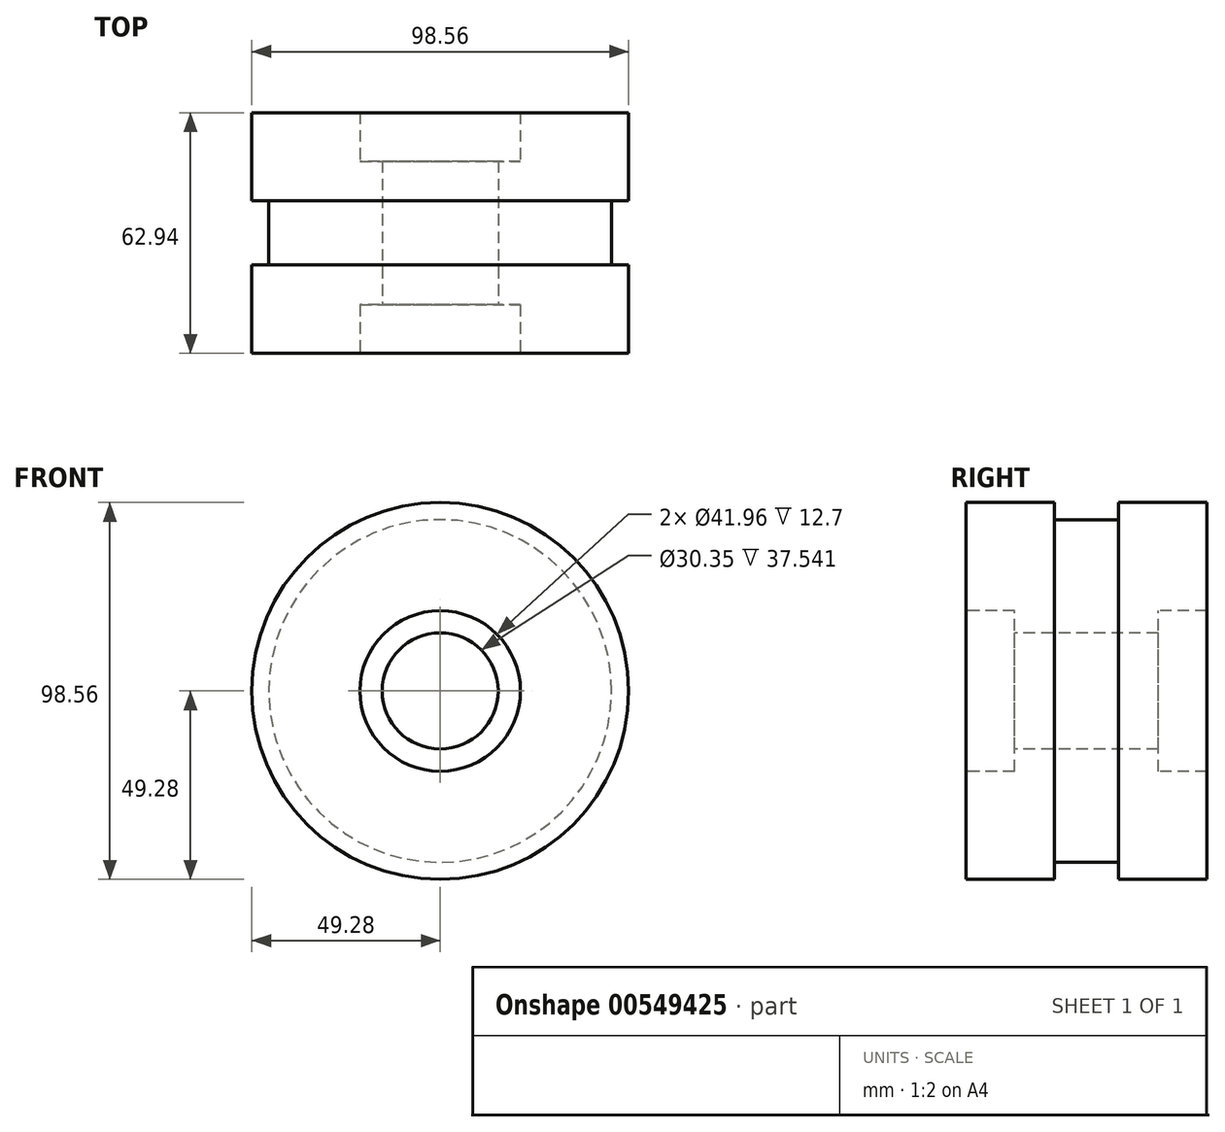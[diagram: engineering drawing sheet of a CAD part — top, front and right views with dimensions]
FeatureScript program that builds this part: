
annotation { "Feature Type Name" : "Feature", "Feature Type Description" : "" }
export const myFeature = defineFeature(function(context is Context, id is Id, definition is map)
    precondition{}
    {
        {
            var Q0;
            Q0=qCreatedBy(makeId("Right.planeOp"),FACE);
            var sketch = newSketch(context, id + "F0", { "sketchPlane" : qUnion([Q0])});
            skLineSegment(sketch, "E0", {"start": v(-35.21, 0) * mm, "end": v(33.24, 0) * mm, "construction": true});
            skLineSegment(sketch, "E1", {"start": v(0, 15.18) * mm, "end": v(-18.77, 15.18) * mm});
            skLineSegment(sketch, "E2", {"start": v(-18.77, 15.18) * mm, "end": v(-18.77, 20.98) * mm});
            skLineSegment(sketch, "E3", {"start": v(-18.77, 20.98) * mm, "end": v(-31.47, 20.98) * mm});
            skLineSegment(sketch, "E4", {"start": v(-31.47, 20.98) * mm, "end": v(-31.47, 49.28) * mm});
            skLineSegment(sketch, "E5", {"start": v(-31.47, 49.28) * mm, "end": v(-8.38, 49.28) * mm});
            skLineSegment(sketch, "E6", {"start": v(-8.38, 49.28) * mm, "end": v(-8.38, 44.8) * mm});
            skLineSegment(sketch, "E7", {"start": v(-8.38, 44.8) * mm, "end": v(8.38, 44.8) * mm});
            skLineSegment(sketch, "E8", {"start": v(0, 44.8) * mm, "end": v(0, 15.18) * mm, "construction": true});
            skLineSegment(sketch, "E9.MirrorCS", {"start": v(8.38, 49.28) * mm, "end": v(8.38, 44.8) * mm});
            skLineSegment(sketch, "E10.MirrorCS", {"start": v(31.47, 49.28) * mm, "end": v(8.38, 49.28) * mm});
            skLineSegment(sketch, "E11.MirrorCS", {"start": v(31.47, 20.98) * mm, "end": v(31.47, 49.28) * mm});
            skLineSegment(sketch, "E12.MirrorCS", {"start": v(18.77, 20.98) * mm, "end": v(31.47, 20.98) * mm});
            skLineSegment(sketch, "E13.MirrorCS", {"start": v(18.77, 15.18) * mm, "end": v(18.77, 20.98) * mm});
            skLineSegment(sketch, "E14.MirrorCS", {"start": v(0, 15.18) * mm, "end": v(18.77, 15.18) * mm});
            skPoint(sketch, "E15.orphan", {"position": v(0, 44.8) * mm});
            skSolve(sketch);
        }
        {
            var Q0;
            Q0=qSketchRegion(id+"F0",true);
            var Q1;
            Q1=sQuery(id+"F0.wireOp",EDGE,"E0");
            revolve(context, id + "F1", {"entities" : qUnion([Q0]), "axis" : qUnion([Q1]), "revolveType" : RevolveType.FULL});
        }
    });
